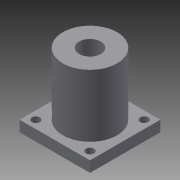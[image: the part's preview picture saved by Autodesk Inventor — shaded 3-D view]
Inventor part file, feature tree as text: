
AUTODESK INVENTOR PART (.ipt)
format: ipt  version: 2014 SP1 (Build 180222100, 222)  size: 106,496 bytes
history: native  units: in
note: dims shown in document units (in); Inventor stores cm internally (conversion verified against a paired STEP export)
features: extrude x3, sketch x3
ambient origin geometry x8: Origin, YZ Plane, XZ Plane, XY Plane, X Axis, Y Axis, Z Axis, Center Point
bodies: Solid1 (feature_tree)
feature tree (6):
  extrude  "Extrusion1"  Depth=1.625in
  extrude  "Extrusion2"  Depth=0.25in
  extrude  "Extrusion3"  Depth=1.4375in TaperAngle=0.0deg
  sketch  "Sketch1"  dims[d0=1.625in d1=1.625in]
  sketch  "Sketch2"  dims[d2=0.25in d3=0.0in d4=0.5in]
  sketch  "Sketch3"  dims[d5=1.25in d6=1.4375in d7=0.0in d8=0.1875in d10=1.25in d11=0.625in d12=0.625in d13=1.4375in d14=0.0in d15=0.5in]
